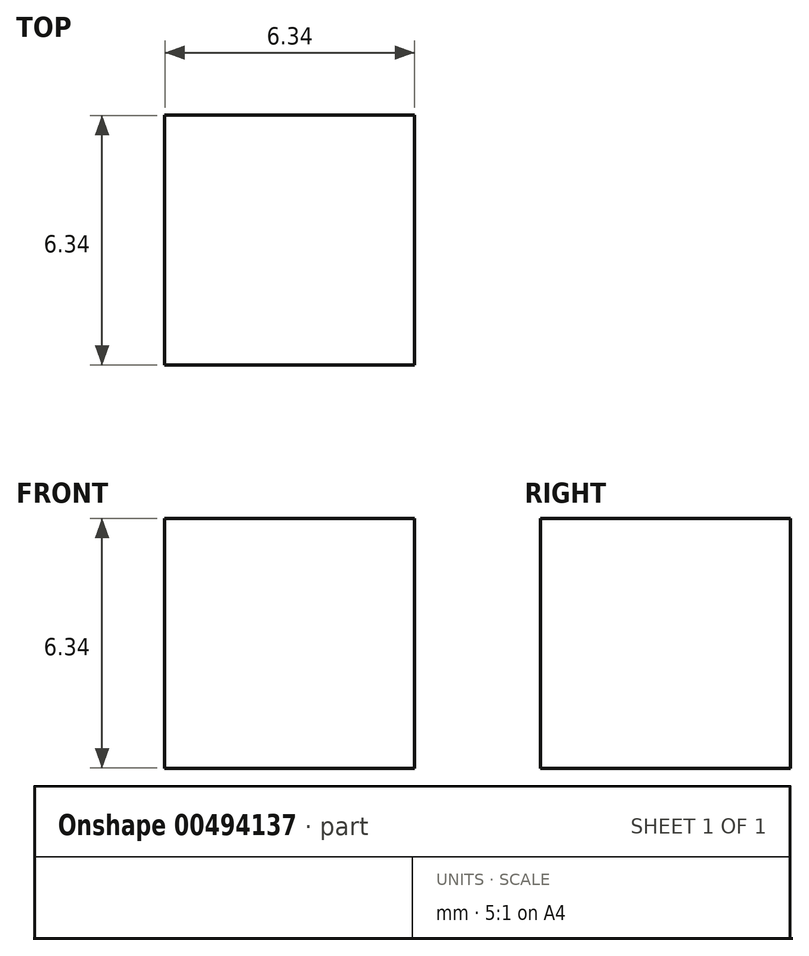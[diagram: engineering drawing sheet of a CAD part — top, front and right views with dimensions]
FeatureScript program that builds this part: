
annotation { "Feature Type Name" : "Feature", "Feature Type Description" : "" }
export const myFeature = defineFeature(function(context is Context, id is Id, definition is map)
    precondition{}
    {
        {
            var Q0;
            Q0=qCreatedBy(makeId("Right.planeOp"),FACE);
            var sketch = newSketch(context, id + "F0", { "sketchPlane" : qUnion([Q0])});
            skLineSegment(sketch, "E0.bottom", {"start": v(-3.17, 3.17) * mm, "end": v(3.18, 3.17) * mm});
            skLineSegment(sketch, "E0.top", {"start": v(-3.17, -3.18) * mm, "end": v(3.18, -3.18) * mm});
            skLineSegment(sketch, "E0.left", {"start": v(-3.17, 3.18) * mm, "end": v(-3.17, -3.18) * mm});
            skLineSegment(sketch, "E0.right", {"start": v(3.18, 3.17) * mm, "end": v(3.18, -3.18) * mm});
            skPoint(sketch, "E0.middle", {"position": v(0, 0) * mm});
            skSolve(sketch);
        }
        {
            var Q0;
            Q0 = qSketchRegion(id + "F0", true);
            extrude(context, id + "F1", {"entities" : qUnion([Q0]), "endBound" : BoundingType.SYMMETRIC, "depth" : 6.35 * mm});
        }
    });
